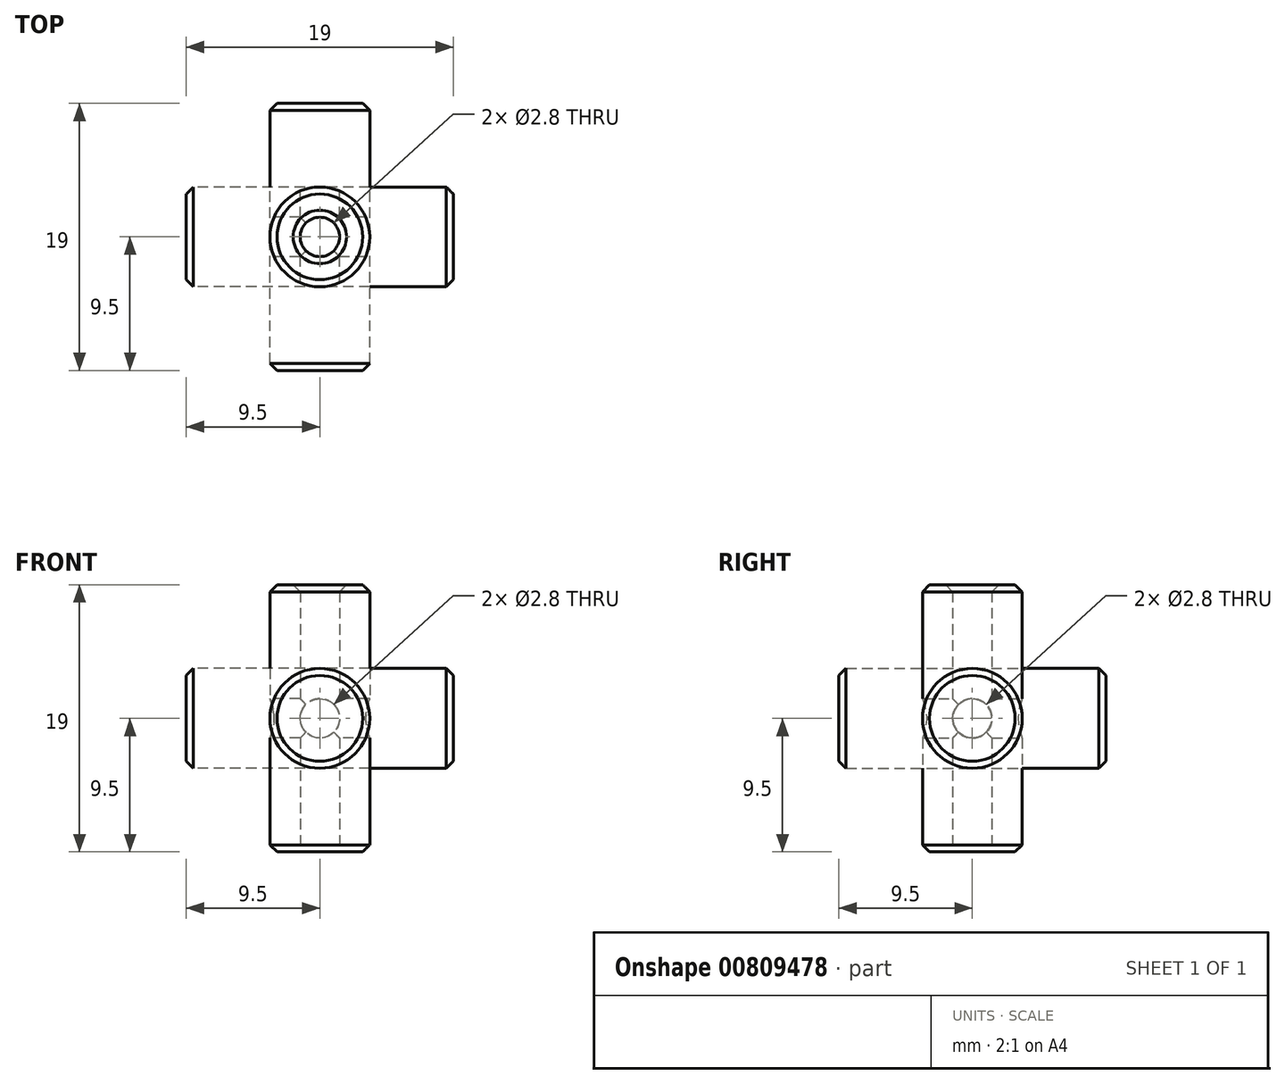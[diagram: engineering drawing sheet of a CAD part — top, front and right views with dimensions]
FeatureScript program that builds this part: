
annotation { "Feature Type Name" : "Feature", "Feature Type Description" : "" }
export const myFeature = defineFeature(function(context is Context, id is Id, definition is map)
    precondition{}
    {
        {
            var Q0;
            Q0=qCreatedBy(makeId("Front.planeOp"),FACE);
            var sketch = newSketch(context, id + "F0", { "sketchPlane" : qUnion([Q0])});
            skCircle(sketch, "E0", {"center": v(0, 0) * mm, "radius": 3.55 * mm});
            skSolve(sketch);
        }
        {
            var Q0;
            Q0=makeQuery(id+"F0.imprint","IMPRINT",FACE,{"disambiguationData":[TD([[makeQuery(id+"F0.imprint","IMPRINT",EDGE,{"derivedFrom":sQuery(id+"F0.wireOp",EDGE,"E0")}),1.0]])]});
            extrude(context, id + "F1", {"entities" : qUnion([Q0]), "endBound" : BoundingType.SYMMETRIC, "depth" : 19 * mm, "offsetDistance" : 25 * mm});
        }
        {
            var Q0;
            Q0=qCreatedBy(makeId("Front.planeOp"),FACE);
            var sketch = newSketch(context, id + "F2", { "sketchPlane" : qUnion([Q0])});
            skCircle(sketch, "E1", {"center": v(0, 0) * mm, "radius": 1.4 * mm});
            skSolve(sketch);
        }
        {
            var Q0;
            Q0 = qSketchRegion(id + "F2", true);
            extrude(context, id + "F3", {"entities" : qUnion([Q0]), "endBound" : BoundingType.SYMMETRIC, "depth" : 20 * mm, "offsetDistance" : 25 * mm});
        }
        {
            var Q0;
            Q0=qCreatedBy(makeId("Front.planeOp"),FACE);
            var sketch = newSketch(context, id + "F4", { "sketchPlane" : qUnion([Q0])});
            skLineSegment(sketch, "E2.bottom", {"start": v(0, 0) * mm, "end": v(10, 0) * mm});
            skLineSegment(sketch, "E2.top", {"start": v(0, 10) * mm, "end": v(10, 10) * mm});
            skLineSegment(sketch, "E2.left", {"start": v(0, 0) * mm, "end": v(0, 10) * mm});
            skLineSegment(sketch, "E2.right", {"start": v(10, 0) * mm, "end": v(10, 10) * mm});
            skSolve(sketch);
        }
        {
            var Q0;
            Q0 = qSketchRegion(id + "F4", true);
            extrude(context, id + "F5", {"entities" : qUnion([Q0]), "depth" : 10 * mm, "offsetDistance" : 25 * mm});
        }
        {
            var Q0;
            Q0=qCreatedBy(makeId("Origin.pointOp"),VERTEX);
            var Q1;
            Q1=makeQuery(id+"F5.opExtrude","CAP_VERTEX",VERTEX,{"disambiguationData":[OSD([sQuery(id+"F4.wireOp",EDGE,"E2.bottom"),sQuery(id+"F4.wireOp",EDGE,"E2.right")])],"isStart":false});
            var Q2;
            Q2=makeQuery(id+"F5.opExtrude","CAP_VERTEX",VERTEX,{"disambiguationData":[OSD([sQuery(id+"F4.wireOp",EDGE,"E2.top"),sQuery(id+"F4.wireOp",EDGE,"E2.right")])],"isStart":false});
            cPlane(context, id + "F6", {"entities" : qUnion([Q0, Q1, Q2]), "cplaneType" : CPlaneType.THREE_POINT, "offset" : 25 * mm, "width" : 150 * mm, "height" : 150 * mm});
        }
        {
            var Q0;
            Q0=qCreatedBy(id+"F6.planeOp",FACE);
            var sketch = newSketch(context, id + "F7", { "sketchPlane" : qUnion([Q0])});
            skLineSegment(sketch, "E3", {"start": v(0, 0) * mm, "end": v(-14.14, 10) * mm});
            skSolve(sketch);
        }
        {
            var Q0;
            Q0=makeQuery(id+"F5.opExtrude","SWEPT_BODY",BODY,{"disambiguationData":[OSD([sQuery(id+"F4.wireOp",EDGE,"E2.bottom"),sQuery(id+"F4.wireOp",EDGE,"E2.top"),sQuery(id+"F4.wireOp",EDGE,"E2.left"),sQuery(id+"F4.wireOp",EDGE,"E2.right")])]});
            deleteBodies(context, id + "F8", {"entities" : qUnion([Q0])});
        }
        {
            var Q0;
            Q0=makeQuery(id+"F1.opExtrude","SWEPT_BODY",BODY,{"disambiguationData":[OSD([sQuery(id+"F0.wireOp",EDGE,"E0")])]});
            var Q1;
            Q1=makeQuery(id+"F3.opExtrude","SWEPT_BODY",BODY,{"disambiguationData":[OSD([sQuery(id+"F2.wireOp",EDGE,"E1")])]});
            var Q2;
            Q2=sQuery(id+"F7.wireOp",EDGE,"E3");
            circularPattern(context, id + "F9", {"entities" : qUnion([Q0, Q1]), "axis" : qUnion([Q2]), "angle" : 360 * degree, "instanceCount" : 3, "equalSpace" : true});
        }
        {
            var Q0;
            Q0=makeQuery(id+"F9.opPattern","COPY",BODY,{"derivedFrom":makeQuery(id+"F3.opExtrude","SWEPT_BODY",BODY,{"disambiguationData":[OSD([sQuery(id+"F2.wireOp",EDGE,"E1")])]}),"instanceName":"2"});
            var Q1;
            Q1=makeQuery(id+"F3.opExtrude","SWEPT_BODY",BODY,{"disambiguationData":[OSD([sQuery(id+"F2.wireOp",EDGE,"E1")])]});
            var Q2;
            Q2=makeQuery(id+"F9.opPattern","COPY",BODY,{"derivedFrom":makeQuery(id+"F3.opExtrude","SWEPT_BODY",BODY,{"disambiguationData":[OSD([sQuery(id+"F2.wireOp",EDGE,"E1")])]}),"instanceName":"1"});
            var Q3;
            Q3=makeQuery(id+"F9.opPattern","COPY",BODY,{"derivedFrom":makeQuery(id+"F1.opExtrude","SWEPT_BODY",BODY,{"disambiguationData":[OSD([sQuery(id+"F0.wireOp",EDGE,"E0")])]}),"instanceName":"2"});
            booleanBodies(context, id + "F10", {"operationType" : BooleanOperationType.SUBTRACTION, "tools" : qUnion([Q0, Q1, Q2]), "targets" : qUnion([Q3])});
        }
        {
            var Q0;
            Q0=makeQuery(id+"F9.opPattern","COPY",FACE,{"derivedFrom":makeQuery(id+"F1.opExtrude","CAP_FACE",FACE,{"disambiguationData":[OSD([sQuery(id+"F0.wireOp",EDGE,"E0")])],"isStart":false}),"instanceName":"2"});
            var Q1;
            Q1=makeQuery(id+"F9.opPattern","COPY",FACE,{"derivedFrom":makeQuery(id+"F1.opExtrude","CAP_FACE",FACE,{"disambiguationData":[OSD([sQuery(id+"F0.wireOp",EDGE,"E0")])],"isStart":true}),"instanceName":"1"});
            var Q2;
            Q2=makeQuery(id+"F1.opExtrude","CAP_FACE",FACE,{"disambiguationData":[OSD([sQuery(id+"F0.wireOp",EDGE,"E0")])],"isStart":true});
            var Q3;
            Q3=makeQuery(id+"F1.opExtrude","CAP_FACE",FACE,{"disambiguationData":[OSD([sQuery(id+"F0.wireOp",EDGE,"E0")])],"isStart":false});
            var Q4;
            Q4=makeQuery(id+"F9.opPattern","COPY",FACE,{"derivedFrom":makeQuery(id+"F1.opExtrude","CAP_FACE",FACE,{"disambiguationData":[OSD([sQuery(id+"F0.wireOp",EDGE,"E0")])],"isStart":false}),"instanceName":"1"});
            var Q5;
            Q5=makeQuery(id+"F9.opPattern","COPY",EDGE,{"derivedFrom":makeQuery(id+"F1.opExtrude","CAP_EDGE",EDGE,{"disambiguationData":[OSD([sQuery(id+"F0.wireOp",EDGE,"E0")])],"isStart":true}),"instanceName":"2"});
            chamfer(context, id + "F11", {"entities" : qUnion([Q0, Q1, Q2, Q3, Q4, Q5]), "width" : 0.5 * mm, "tangentPropagation" : true});
        }
    });
